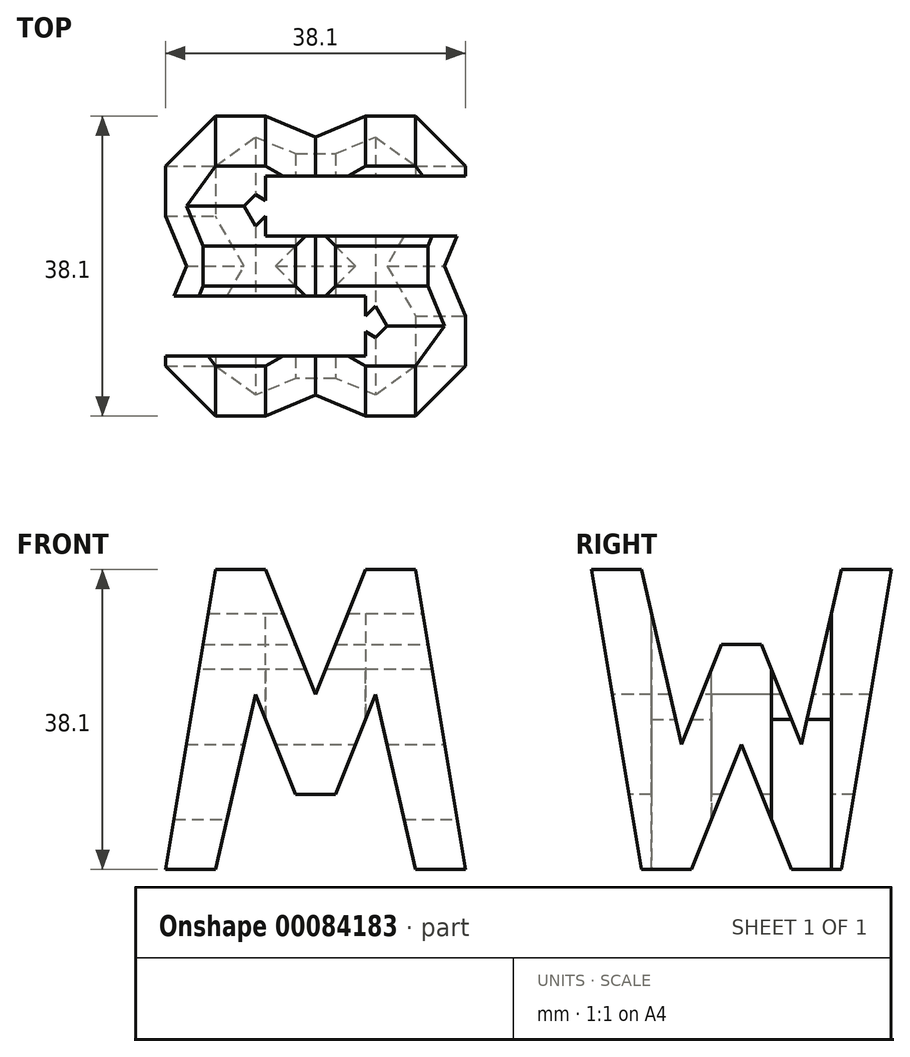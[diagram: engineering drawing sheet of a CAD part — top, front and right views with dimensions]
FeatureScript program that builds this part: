
annotation { "Feature Type Name" : "Feature", "Feature Type Description" : "" }
export const myFeature = defineFeature(function(context is Context, id is Id, definition is map)
    precondition{}
    {
        {
            var Q0;
            Q0=qCreatedBy(makeId("Front.planeOp"),FACE);
            var sketch = newSketch(context, id + "F0", { "sketchPlane" : qUnion([Q0])});
            skLineSegment(sketch, "E0", {"start": v(0, 0) * mm, "end": v(0, 38.1) * mm});
            skLineSegment(sketch, "E1", {"start": v(38.1, 38.1) * mm, "end": v(0, 38.1) * mm});
            skLineSegment(sketch, "E2", {"start": v(38.1, 38.1) * mm, "end": v(38.1, 0) * mm});
            skLineSegment(sketch, "E3", {"start": v(0, 0) * mm, "end": v(38.1, 0) * mm});
            skSolve(sketch);
        }
        {
            var Q0;
            Q0 = qSketchRegion(id + "F0", true);
            extrude(context, id + "F1", {"entities" : qUnion([Q0]), "depth" : 38.1 * mm});
        }
        {
            var Q0;
            Q0=qCreatedBy(makeId("Front.planeOp"),FACE);
            cPlane(context, id + "F2", {"entities" : qUnion([Q0]), "cplaneType" : CPlaneType.OFFSET, "offset" : 38.1 * mm, "width" : 152.4 * mm, "height" : 152.4 * mm});
        }
        {
            var Q0;
            Q0=qCreatedBy(makeId("Top.planeOp"),FACE);
            cPlane(context, id + "F3", {"entities" : qUnion([Q0]), "cplaneType" : CPlaneType.OFFSET, "offset" : 38.1 * mm, "width" : 152.4 * mm, "height" : 152.4 * mm});
        }
        {
            var Q0;
            Q0=qCreatedBy(makeId("Right.planeOp"),FACE);
            cPlane(context, id + "F4", {"entities" : qUnion([Q0]), "cplaneType" : CPlaneType.OFFSET, "offset" : 38.1 * mm, "width" : 152.4 * mm, "height" : 152.4 * mm});
        }
        {
            var Q0;
            Q0=qCreatedBy(id+"F4.planeOp",FACE);
            var sketch = newSketch(context, id + "F5", { "sketchPlane" : qUnion([Q0])});
            skLineSegment(sketch, "E4", {"start": v(0, 0) * mm, "end": v(0, 38.1) * mm});
            skLineSegment(sketch, "E5", {"start": v(0, 38.1) * mm, "end": v(-38.1, 38.1) * mm});
            skLineSegment(sketch, "E6", {"start": v(-38.1, 38.1) * mm, "end": v(-38.1, 0) * mm});
            skLineSegment(sketch, "E7", {"start": v(-38.1, 0) * mm, "end": v(0, 0) * mm});
            skLineSegment(sketch, "E8", {"start": v(-38.1, 38.1) * mm, "end": v(-31.75, 0) * mm});
            skLineSegment(sketch, "E9", {"start": v(-31.75, 0) * mm, "end": v(-25.4, 0) * mm});
            skLineSegment(sketch, "E10", {"start": v(-25.4, 0) * mm, "end": v(-19.05, 15.88) * mm});
            skLineSegment(sketch, "E11", {"start": v(-19.05, 15.88) * mm, "end": v(-12.7, 0) * mm});
            skLineSegment(sketch, "E12", {"start": v(-12.7, 0) * mm, "end": v(-6.35, 0) * mm});
            skLineSegment(sketch, "E13", {"start": v(-6.35, 0) * mm, "end": v(0, 38.1) * mm});
            skLineSegment(sketch, "E14", {"start": v(-6.35, 38.1) * mm, "end": v(-11.43, 15.87) * mm});
            skLineSegment(sketch, "E15", {"start": v(-11.43, 15.87) * mm, "end": v(-16.5, 28.58) * mm});
            skLineSegment(sketch, "E16", {"start": v(-16.5, 28.58) * mm, "end": v(-21.59, 28.58) * mm});
            skLineSegment(sketch, "E17", {"start": v(-21.59, 28.58) * mm, "end": v(-26.67, 15.87) * mm});
            skLineSegment(sketch, "E18", {"start": v(-26.67, 15.88) * mm, "end": v(-31.75, 38.1) * mm});
            skLineSegment(sketch, "E19", {"start": v(-31.75, 38.1) * mm, "end": v(-38.1, 38.1) * mm});
            skSolve(sketch);
        }
        {
            var Q0;
            {var subQ0=sQuery(id+"F5.wireOp",EDGE,"E14");Q0=makeQuery(id+"F5.imprint","IMPRINT",FACE,{"disambiguationData":[TD([[makeQuery(id+"F5.imprint","IMPRINT",EDGE,{"derivedFrom":subQ0}),-1.0]])]});}
            var Q1;
            {var subQ0=sQuery(id+"F5.wireOp",EDGE,"E6");Q1=makeQuery(id+"F5.imprint","IMPRINT",FACE,{"disambiguationData":[TD([[makeQuery(id+"F5.imprint","IMPRINT",EDGE,{"derivedFrom":subQ0}),1.0]])]});}
            var Q2;
            {var subQ0=sQuery(id+"F5.wireOp",EDGE,"E10");Q2=makeQuery(id+"F5.imprint","IMPRINT",FACE,{"disambiguationData":[TD([[makeQuery(id+"F5.imprint","IMPRINT",EDGE,{"derivedFrom":subQ0}),-1.0]])]});}
            var Q3;
            {var subQ0=sQuery(id+"F5.wireOp",EDGE,"E4");Q3=makeQuery(id+"F5.imprint","IMPRINT",FACE,{"disambiguationData":[TD([[makeQuery(id+"F5.imprint","IMPRINT",EDGE,{"derivedFrom":subQ0}),1.0]])]});}
            extrude(context, id + "F6", {"entities" : qUnion([Q0, Q1, Q2, Q3]), "operationType" : NewBodyOperationType.REMOVE, "oppositeDirection" : true, "depth" : 38.1 * mm});
        }
        {
            var Q0;
            Q0=qCreatedBy(id+"F2.planeOp",FACE);
            var sketch = newSketch(context, id + "F7", { "sketchPlane" : qUnion([Q0])});
            skLineSegment(sketch, "E20", {"start": v(0, 0) * mm, "end": v(38.1, 0) * mm});
            skLineSegment(sketch, "E21", {"start": v(38.1, 0) * mm, "end": v(38.1, 38.1) * mm});
            skLineSegment(sketch, "E22", {"start": v(38.1, 38.1) * mm, "end": v(0, 38.1) * mm});
            skLineSegment(sketch, "E23", {"start": v(0, 38.1) * mm, "end": v(0, 0) * mm});
            skLineSegment(sketch, "E24", {"start": v(0, 0) * mm, "end": v(6.35, 38.1) * mm});
            skLineSegment(sketch, "E25", {"start": v(6.35, 38.1) * mm, "end": v(12.7, 38.1) * mm});
            skLineSegment(sketch, "E26", {"start": v(12.7, 38.1) * mm, "end": v(19.05, 22.23) * mm});
            skLineSegment(sketch, "E27", {"start": v(19.05, 22.23) * mm, "end": v(25.4, 38.1) * mm});
            skLineSegment(sketch, "E28", {"start": v(25.4, 38.1) * mm, "end": v(31.75, 38.1) * mm});
            skLineSegment(sketch, "E29", {"start": v(31.75, 38.1) * mm, "end": v(38.1, 0) * mm});
            skLineSegment(sketch, "E30", {"start": v(31.75, 0) * mm, "end": v(26.67, 22.23) * mm});
            skLineSegment(sketch, "E31", {"start": v(26.67, 22.23) * mm, "end": v(21.59, 9.53) * mm});
            skLineSegment(sketch, "E32", {"start": v(21.59, 9.53) * mm, "end": v(16.51, 9.53) * mm});
            skLineSegment(sketch, "E33", {"start": v(16.51, 9.53) * mm, "end": v(11.43, 22.23) * mm});
            skLineSegment(sketch, "E34", {"start": v(11.43, 22.23) * mm, "end": v(6.35, 0) * mm});
            skLineSegment(sketch, "E35", {"start": v(6.35, 0) * mm, "end": v(0, 0) * mm});
            skSolve(sketch);
        }
        {
            var Q0;
            {var subQ0=sQuery(id+"F7.wireOp",EDGE,"E26");Q0=makeQuery(id+"F7.imprint","IMPRINT",FACE,{"disambiguationData":[TD([[makeQuery(id+"F7.imprint","IMPRINT",EDGE,{"derivedFrom":subQ0}),1.0]])]});}
            var Q1;
            {var subQ0=sQuery(id+"F7.wireOp",EDGE,"E23");Q1=makeQuery(id+"F7.imprint","IMPRINT",FACE,{"disambiguationData":[TD([[makeQuery(id+"F7.imprint","IMPRINT",EDGE,{"derivedFrom":subQ0}),1.0]])]});}
            var Q2;
            {var subQ2=sQuery(id+"F7.wireOp",EDGE,"E30");Q2=makeQuery(id+"F7.imprint","IMPRINT",FACE,{"disambiguationData":[TD([[makeQuery(id+"F7.imprint","IMPRINT",EDGE,{"derivedFrom":subQ2}),1.0]])]});}
            var Q3;
            {var subQ0=sQuery(id+"F7.wireOp",EDGE,"E21");Q3=makeQuery(id+"F7.imprint","IMPRINT",FACE,{"disambiguationData":[TD([[makeQuery(id+"F7.imprint","IMPRINT",EDGE,{"derivedFrom":subQ0}),1.0]])]});}
            extrude(context, id + "F8", {"entities" : qUnion([Q0, Q1, Q2, Q3]), "operationType" : NewBodyOperationType.REMOVE, "oppositeDirection" : true, "depth" : 38.1 * mm});
        }
        {
            var Q0;
            Q0=qCreatedBy(id+"F3.planeOp",FACE);
            var sketch = newSketch(context, id + "F9", { "sketchPlane" : qUnion([Q0])});
            skLineSegment(sketch, "E36", {"start": v(0, 0) * mm, "end": v(38.1, 0) * mm});
            skLineSegment(sketch, "E37", {"start": v(38.1, 0) * mm, "end": v(38.1, -38.1) * mm});
            skLineSegment(sketch, "E38", {"start": v(38.1, -38.1) * mm, "end": v(0, -38.1) * mm});
            skLineSegment(sketch, "E39", {"start": v(0, -38.1) * mm, "end": v(0, 0) * mm});
            skLineSegment(sketch, "E40", {"start": v(0, -30.48) * mm, "end": v(25.4, -30.48) * mm});
            skLineSegment(sketch, "E41", {"start": v(25.4, -30.48) * mm, "end": v(25.4, -22.86) * mm});
            skLineSegment(sketch, "E42", {"start": v(25.4, -22.86) * mm, "end": v(0, -22.86) * mm});
            skLineSegment(sketch, "E43", {"start": v(38.1, -15.24) * mm, "end": v(12.7, -15.24) * mm});
            skLineSegment(sketch, "E44", {"start": v(12.7, -15.24) * mm, "end": v(12.7, -7.62) * mm});
            skLineSegment(sketch, "E45", {"start": v(12.7, -7.62) * mm, "end": v(38.1, -7.62) * mm});
            skSolve(sketch);
        }
        {
            var Q0;
            {var subQ0=sQuery(id+"F9.wireOp",EDGE,"E40");Q0=makeQuery(id+"F9.imprint","IMPRINT",FACE,{"disambiguationData":[TD([[makeQuery(id+"F9.imprint","IMPRINT",EDGE,{"derivedFrom":subQ0}),1.0]])]});}
            var Q1;
            {var subQ0=sQuery(id+"F9.wireOp",EDGE,"E43");Q1=makeQuery(id+"F9.imprint","IMPRINT",FACE,{"disambiguationData":[TD([[makeQuery(id+"F9.imprint","IMPRINT",EDGE,{"derivedFrom":subQ0}),-1.0]])]});}
            extrude(context, id + "F10", {"entities" : qUnion([Q0, Q1]), "operationType" : NewBodyOperationType.REMOVE, "oppositeDirection" : true, "depth" : 38.1 * mm});
        }
    });
